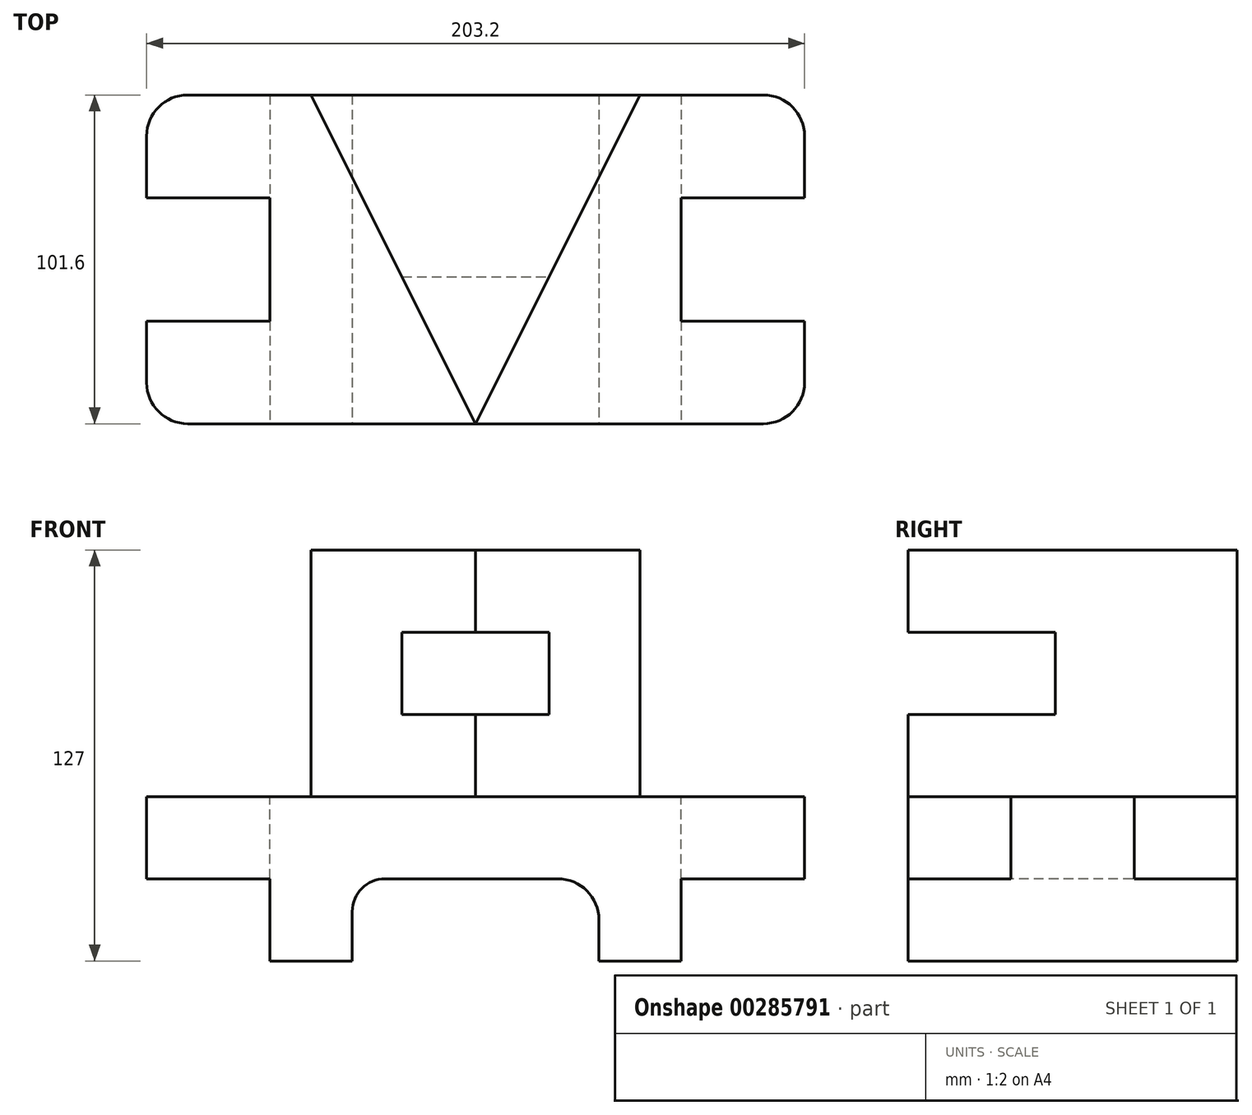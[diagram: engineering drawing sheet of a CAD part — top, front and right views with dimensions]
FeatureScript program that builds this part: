
annotation { "Feature Type Name" : "Feature", "Feature Type Description" : "" }
export const myFeature = defineFeature(function(context is Context, id is Id, definition is map)
    precondition{}
    {
        {
            var Q0;
            Q0=qCreatedBy(makeId("Front.planeOp"),FACE);
            var sketch = newSketch(context, id + "F0", { "sketchPlane" : qUnion([Q0])});
            skLineSegment(sketch, "E0.bottom", {"start": v(0, 0) * mm, "end": v(203.2, 0) * mm});
            skLineSegment(sketch, "E0.top", {"start": v(0, 25.4) * mm, "end": v(203.2, 25.4) * mm});
            skLineSegment(sketch, "E0.left", {"start": v(0, 0) * mm, "end": v(0, 25.4) * mm});
            skLineSegment(sketch, "E0.right", {"start": v(203.2, 0) * mm, "end": v(203.2, 25.4) * mm});
            skSolve(sketch);
        }
        {
            var Q0;
            Q0 = qSketchRegion(id + "F0", true);
            extrude(context, id + "F1", {"entities" : qUnion([Q0]), "endBound" : BoundingType.SYMMETRIC, "depth" : 101.6 * mm});
        }
        {
            var Q0;
            Q0=makeQuery(id+"F1.opExtrude","SWEPT_FACE",FACE,{"disambiguationData":[OSD([sQuery(id+"F0.wireOp",EDGE,"E0.top")])]});
            var sketch = newSketch(context, id + "F2", { "sketchPlane" : qUnion([Q0])});
            skLineSegment(sketch, "E1", {"start": v(101.6, -50.8) * mm, "end": v(50.8, 50.8) * mm});
            skLineSegment(sketch, "E2", {"start": v(50.8, 50.8) * mm, "end": v(152.4, 50.8) * mm});
            skLineSegment(sketch, "E3", {"start": v(152.4, 50.8) * mm, "end": v(101.6, -50.8) * mm});
            skSolve(sketch);
        }
        {
            var Q0;
            Q0 = qSketchRegion(id + "F2", true);
            extrude(context, id + "F3", {"entities" : qUnion([Q0]), "operationType" : NewBodyOperationType.ADD, "depth" : 25.4 * mm});
        }
        {
            var Q0;
            Q0=makeQuery(id+"F3.opExtrude","CAP_FACE",FACE,{"disambiguationData":[OSD([sQuery(id+"F2.wireOp",EDGE,"E1"),sQuery(id+"F2.wireOp",EDGE,"E2"),sQuery(id+"F2.wireOp",EDGE,"E3")])],"isStart":false});
            var sketch = newSketch(context, id + "F4", { "sketchPlane" : qUnion([Q0])});
            skLineSegment(sketch, "E4", {"start": v(101.6, -50.8) * mm, "end": v(78.88, -5.36) * mm});
            skLineSegment(sketch, "E5", {"start": v(78.88, -5.36) * mm, "end": v(124.32, -5.36) * mm});
            skLineSegment(sketch, "E6", {"start": v(124.32, -5.36) * mm, "end": v(101.6, -50.8) * mm});
            skSolve(sketch);
        }
        {
            var Q0;
            {var subQ0=sQuery(id+"F4.wireOp",EDGE,"E5");Q0=makeQuery(id+"F4.imprint","IMPRINT",FACE,{"disambiguationData":[TD([[makeQuery(id+"F4.imprint","IMPRINT",EDGE,{"derivedFrom":subQ0}),1.0]])]});}
            extrude(context, id + "F5", {"entities" : qUnion([Q0]), "operationType" : NewBodyOperationType.ADD, "depth" : 50.8 * mm});
        }
        {
            var Q0;
            Q0=makeQuery(id+"F5.opExtrude","CAP_FACE",FACE,{"disambiguationData":[OSD([sQuery(id+"F2.wireOp",EDGE,"E1"),sQuery(id+"F2.wireOp",EDGE,"E2"),sQuery(id+"F2.wireOp",EDGE,"E3"),sQuery(id+"F4.wireOp",EDGE,"E5")])],"isStart":false});
            var sketch = newSketch(context, id + "F6", { "sketchPlane" : qUnion([Q0])});
            skLineSegment(sketch, "E7", {"start": v(78.88, -5.36) * mm, "end": v(101.6, -50.8) * mm});
            skLineSegment(sketch, "E8", {"start": v(101.6, -50.8) * mm, "end": v(124.32, -5.36) * mm});
            skLineSegment(sketch, "E9", {"start": v(124.32, -5.36) * mm, "end": v(78.88, -5.36) * mm});
            skSolve(sketch);
        }
        {
            var Q0;
            Q0=makeQuery(id+"F6.imprint","IMPRINT",FACE,{"disambiguationData":[TD([[makeQuery(id+"F6.imprint","IMPRINT",EDGE,{"derivedFrom":sQuery(id+"F6.wireOp",EDGE,"E7")}),1.0]])]});
            var Q1;
            Q1=makeQuery(id+"F6.imprint","IMPRINT",FACE,{"disambiguationData":[TD([[makeQuery(id+"F6.imprint","IMPRINT",EDGE,{"derivedFrom":sQuery(id+"F6.wireOp",EDGE,"E9")}),1.0]])]});
            extrude(context, id + "F7", {"entities" : qUnion([Q0, Q1]), "operationType" : NewBodyOperationType.ADD, "oppositeDirection" : true, "depth" : 25.4 * mm});
        }
        {
            var Q0;
            {var subQ0=sQuery(id+"F0.wireOp",EDGE,"E0.right");var subQ1=sQuery(id+"F0.wireOp",EDGE,"E0.top");var subQ2=makeQuery(id+"F1.opExtrude","SWEPT_FACE",FACE,{"disambiguationData":[OSD([subQ1])]});Q0=makeQuery(id+"F3.boolean.opBoolean","SPLIT",FACE,{"disambiguationData":[TD([makeQuery(id+"F1.opExtrude","SWEPT_FACE",FACE,{"disambiguationData":[OSD([subQ0])]})])],"derivedFrom":subQ2});}
            var sketch = newSketch(context, id + "F8", { "sketchPlane" : qUnion([Q0])});
            skLineSegment(sketch, "E10.bottom", {"start": v(0, 19.05) * mm, "end": v(38.1, 19.05) * mm});
            skLineSegment(sketch, "E10.top", {"start": v(0, -19.05) * mm, "end": v(38.1, -19.05) * mm});
            skLineSegment(sketch, "E10.left", {"start": v(0, 19.05) * mm, "end": v(0, -19.05) * mm});
            skLineSegment(sketch, "E10.right", {"start": v(38.1, 19.05) * mm, "end": v(38.1, -19.05) * mm});
            skLineSegment(sketch, "E11.bottom", {"start": v(203.2, -19.05) * mm, "end": v(165.1, -19.05) * mm});
            skLineSegment(sketch, "E11.top", {"start": v(203.2, 19.05) * mm, "end": v(165.1, 19.05) * mm});
            skLineSegment(sketch, "E11.left", {"start": v(203.2, -19.05) * mm, "end": v(203.2, 19.05) * mm});
            skLineSegment(sketch, "E11.right", {"start": v(165.1, -19.05) * mm, "end": v(165.1, 19.05) * mm});
            skSolve(sketch);
        }
        {
            var Q0;
            Q0=makeQuery(id+"F8.imprint","IMPRINT",FACE,{"disambiguationData":[TD([[makeQuery(id+"F8.imprint","IMPRINT",EDGE,{"derivedFrom":sQuery(id+"F8.wireOp",EDGE,"E10.bottom")}),-1.0]])]});
            var Q1;
            Q1=makeQuery(id+"F8.imprint","IMPRINT",FACE,{"disambiguationData":[TD([[makeQuery(id+"F8.imprint","IMPRINT",EDGE,{"derivedFrom":sQuery(id+"F8.wireOp",EDGE,"E11.bottom")}),-1.0]])]});
            extrude(context, id + "F9", {"entities" : qUnion([Q0, Q1]), "operationType" : NewBodyOperationType.REMOVE, "endBound" : BoundingType.THROUGH_ALL, "oppositeDirection" : true, "depth" : 25.4 * mm});
        }
        {
            var Q0;
            Q0=makeQuery(id+"F1.opExtrude","CAP_EDGE",EDGE,{"disambiguationData":[OSD([sQuery(id+"F0.wireOp",EDGE,"E0.left")])],"isStart":true});
            var Q1;
            Q1=makeQuery(id+"F1.opExtrude","CAP_EDGE",EDGE,{"disambiguationData":[OSD([sQuery(id+"F0.wireOp",EDGE,"E0.left")])],"isStart":false});
            var Q2;
            Q2=makeQuery(id+"F1.opExtrude","CAP_EDGE",EDGE,{"disambiguationData":[OSD([sQuery(id+"F0.wireOp",EDGE,"E0.right")])],"isStart":false});
            var Q3;
            Q3=makeQuery(id+"F1.opExtrude","CAP_EDGE",EDGE,{"disambiguationData":[OSD([sQuery(id+"F0.wireOp",EDGE,"E0.right")])],"isStart":true});
            fillet(context, id + "F10", {"entities" : qUnion([Q0, Q1, Q2, Q3]), "radius" : 12.7 * mm, "tangentPropagation" : true, "allowEdgeOverflow" : false});
        }
        {
            var Q0;
            Q0=makeQuery(id+"F1.opExtrude","CAP_FACE",FACE,{"disambiguationData":[OSD([sQuery(id+"F0.wireOp",EDGE,"E0.bottom"),sQuery(id+"F0.wireOp",EDGE,"E0.top"),sQuery(id+"F0.wireOp",EDGE,"E0.left"),sQuery(id+"F0.wireOp",EDGE,"E0.right")])],"isStart":false});
            var sketch = newSketch(context, id + "F11", { "sketchPlane" : qUnion([Q0])});
            skLineSegment(sketch, "E12.bottom", {"start": v(38.1, 0) * mm, "end": v(165.1, 0) * mm});
            skLineSegment(sketch, "E12.top", {"start": v(38.1, -25.4) * mm, "end": v(165.1, -25.4) * mm});
            skLineSegment(sketch, "E12.left", {"start": v(38.1, 0) * mm, "end": v(38.1, -25.4) * mm});
            skLineSegment(sketch, "E12.right", {"start": v(165.1, 0) * mm, "end": v(165.1, -25.4) * mm});
            skSolve(sketch);
        }
        {
            var Q0;
            Q0 = qSketchRegion(id + "F11", true);
            var Q1;
            {var subQ0=sQuery(id+"F2.wireOp",EDGE,"E2");Q1=makeQuery(id+"F5.boolean.opBoolean","MERGE",FACE,{"derivedFrom":[makeQuery(id+"F3.boolean.opBoolean","MERGE",FACE,{"derivedFrom":[makeQuery(id+"F1.opExtrude","CAP_FACE",FACE,{"disambiguationData":[OSD([sQuery(id+"F0.wireOp",EDGE,"E0.bottom"),sQuery(id+"F0.wireOp",EDGE,"E0.top"),sQuery(id+"F0.wireOp",EDGE,"E0.left"),sQuery(id+"F0.wireOp",EDGE,"E0.right")])],"isStart":true}),makeQuery(id+"F3.opExtrude","SWEPT_FACE",FACE,{"disambiguationData":[OSD([subQ0])]})]}),makeQuery(id+"F5.opExtrude","SWEPT_FACE",FACE,{"disambiguationData":[OSD([subQ0])]})]});}
            extrude(context, id + "F12", {"entities" : qUnion([Q0]), "operationType" : NewBodyOperationType.ADD, "endBound" : BoundingType.UP_TO_SURFACE, "oppositeDirection" : true, "endBoundEntityFace" : qUnion([Q1]), "depth" : 25.4 * mm});
        }
        {
            var Q0;
            Q0=makeQuery(id+"F12.boolean.opBoolean","MERGE",FACE,{"derivedFrom":[makeQuery(id+"F1.opExtrude","CAP_FACE",FACE,{"disambiguationData":[OSD([sQuery(id+"F0.wireOp",EDGE,"E0.bottom"),sQuery(id+"F0.wireOp",EDGE,"E0.top"),sQuery(id+"F0.wireOp",EDGE,"E0.left"),sQuery(id+"F0.wireOp",EDGE,"E0.right")])],"isStart":false}),makeQuery(id+"F12.opExtrude","CAP_FACE",FACE,{"disambiguationData":[OSD([sQuery(id+"F11.wireOp",EDGE,"E12.bottom"),sQuery(id+"F11.wireOp",EDGE,"E12.top"),sQuery(id+"F11.wireOp",EDGE,"E12.left"),sQuery(id+"F11.wireOp",EDGE,"E12.right")])],"isStart":true})]});
            var sketch = newSketch(context, id + "F13", { "sketchPlane" : qUnion([Q0])});
            skLineSegment(sketch, "E13.bottom", {"start": v(63.5, -25.4) * mm, "end": v(139.7, -25.4) * mm});
            skLineSegment(sketch, "E13.top", {"start": v(63.5, 0) * mm, "end": v(139.7, 0) * mm});
            skLineSegment(sketch, "E13.left", {"start": v(63.5, -25.4) * mm, "end": v(63.5, 0) * mm});
            skLineSegment(sketch, "E13.right", {"start": v(139.7, -25.4) * mm, "end": v(139.7, 0) * mm});
            skSolve(sketch);
        }
        {
            var Q0;
            Q0=makeQuery(id+"F13.imprint","IMPRINT",FACE,{"disambiguationData":[TD([[makeQuery(id+"F13.imprint","IMPRINT",EDGE,{"derivedFrom":sQuery(id+"F13.wireOp",EDGE,"E13.bottom")}),1.0]])]});
            extrude(context, id + "F14", {"entities" : qUnion([Q0]), "operationType" : NewBodyOperationType.REMOVE, "endBound" : BoundingType.THROUGH_ALL, "oppositeDirection" : true, "depth" : 25.4 * mm});
        }
        {
            var Q0;
            Q0=makeQuery(id+"F14.boolean.opBoolean","COPY",EDGE,{"derivedFrom":makeQuery(id+"F14.opExtrude","SWEPT_EDGE",EDGE,{"disambiguationData":[OSD([sQuery(id+"F13.wireOp",EDGE,"E13.top"),sQuery(id+"F13.wireOp",EDGE,"E13.left")])]})});
            fillet(context, id + "F15", {"entities" : qUnion([Q0]), "radius" : 10.16 * mm, "tangentPropagation" : true, "allowEdgeOverflow" : false});
        }
        {
            var Q0;
            Q0=makeQuery(id+"F14.boolean.opBoolean","COPY",EDGE,{"derivedFrom":makeQuery(id+"F14.opExtrude","SWEPT_EDGE",EDGE,{"disambiguationData":[OSD([sQuery(id+"F13.wireOp",EDGE,"E13.top"),sQuery(id+"F13.wireOp",EDGE,"E13.right")])]})});
            fillet(context, id + "F16", {"entities" : qUnion([Q0]), "radius" : 12.7 * mm, "tangentPropagation" : true, "allowEdgeOverflow" : false});
        }
    });
